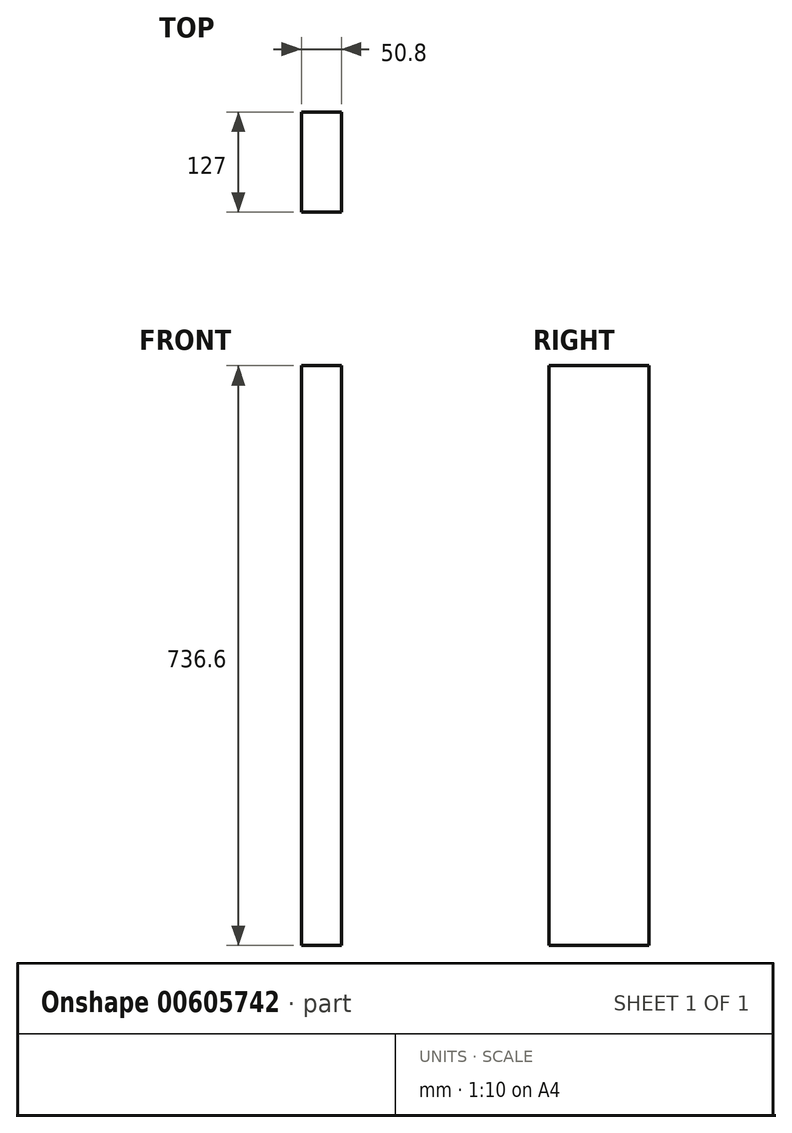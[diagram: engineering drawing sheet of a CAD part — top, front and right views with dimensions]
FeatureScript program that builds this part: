
annotation { "Feature Type Name" : "Feature", "Feature Type Description" : "" }
export const myFeature = defineFeature(function(context is Context, id is Id, definition is map)
    precondition{}
    {
        {
            var Q0;
            Q0=qCreatedBy(makeId("Top.planeOp"),FACE);
            var sketch = newSketch(context, id + "F0", { "sketchPlane" : qUnion([Q0])});
            skLineSegment(sketch, "E0.bottom", {"start": v(4.48, -22.18) * mm, "end": v(55.28, -22.18) * mm});
            skLineSegment(sketch, "E0.top", {"start": v(4.48, 104.82) * mm, "end": v(55.28, 104.82) * mm});
            skLineSegment(sketch, "E0.left", {"start": v(4.48, -22.18) * mm, "end": v(4.48, 104.82) * mm});
            skLineSegment(sketch, "E0.right", {"start": v(55.28, -22.18) * mm, "end": v(55.28, 104.82) * mm});
            skPoint(sketch, "E0.middle", {"position": v(29.88, 41.32) * mm});
            skSolve(sketch);
        }
        {
            var Q0;
            Q0 = qSketchRegion(id + "F0", true);
            extrude(context, id + "F1", {"entities" : qUnion([Q0]), "oppositeDirection" : true, "depth" : 736.6 * mm, "offsetDistance" : 25.4 * mm});
        }
    });
